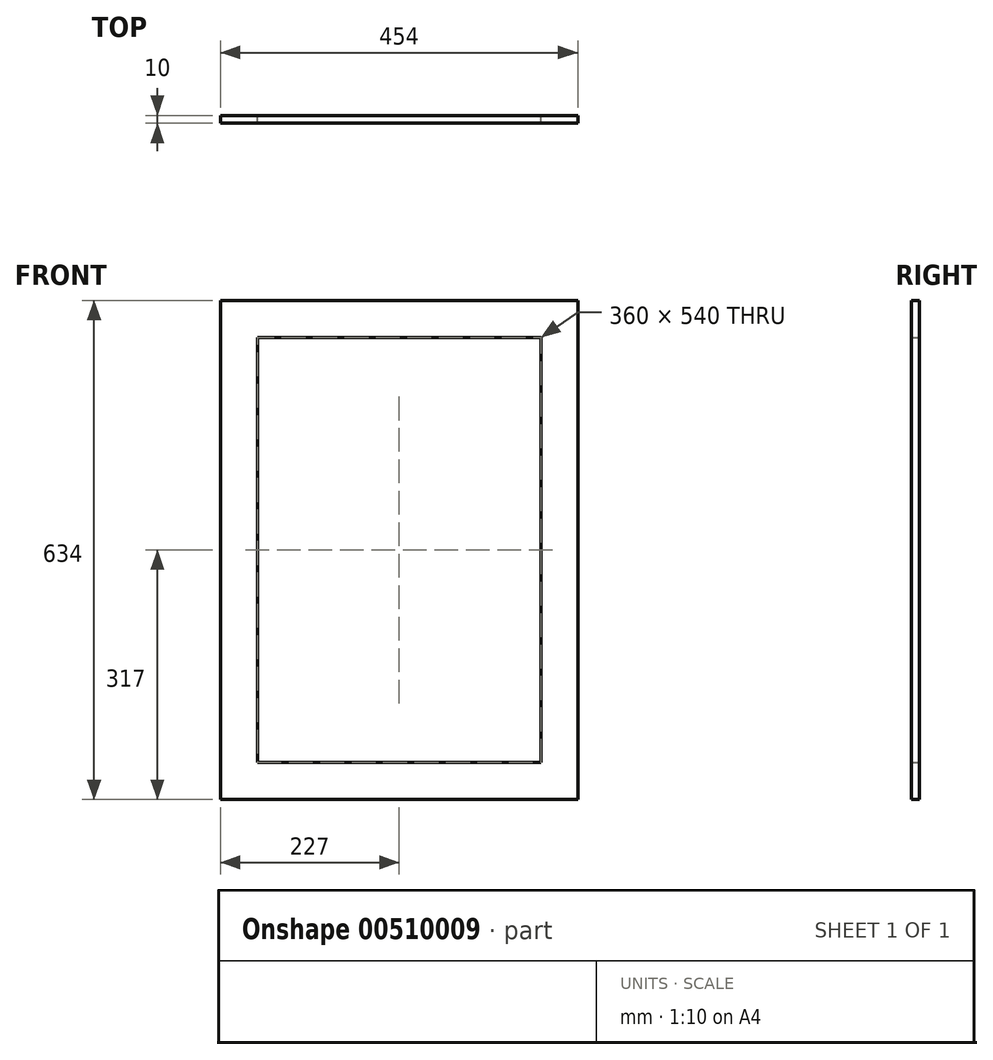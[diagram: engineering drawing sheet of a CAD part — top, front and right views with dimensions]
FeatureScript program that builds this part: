
annotation { "Feature Type Name" : "Feature", "Feature Type Description" : "" }
export const myFeature = defineFeature(function(context is Context, id is Id, definition is map)
    precondition{}
    {
        {
            var Q0;
            Q0=qCreatedBy(makeId("Front.planeOp"),FACE);
            var sketch = newSketch(context, id + "F0", { "sketchPlane" : qUnion([Q0])});
            skLineSegment(sketch, "E0.bottom", {"start": v(-180, 270) * mm, "end": v(180, 270) * mm});
            skLineSegment(sketch, "E0.top", {"start": v(-180, -270) * mm, "end": v(180, -270) * mm});
            skLineSegment(sketch, "E0.left", {"start": v(-180, 270) * mm, "end": v(-180, -270) * mm});
            skLineSegment(sketch, "E0.right", {"start": v(180, 270) * mm, "end": v(180, -270) * mm});
            skLineSegment(sketch, "E1", {"start": v(-180, 270) * mm, "end": v(180, -270) * mm, "construction": true});
            skLineSegment(sketch, "E2.0", {"start": v(-227, 317) * mm, "end": v(227, 317) * mm});
            skLineSegment(sketch, "E2.1", {"start": v(-227, 317) * mm, "end": v(-227, -317) * mm});
            skLineSegment(sketch, "E2.2", {"start": v(-227, -317) * mm, "end": v(227, -317) * mm});
            skLineSegment(sketch, "E2.3", {"start": v(227, 317) * mm, "end": v(227, -317) * mm});
            skSolve(sketch);
        }
        {
            var Q0;
            Q0=qSketchRegion(id+"F0",true);
            extrude(context, id + "F1", {"entities" : qUnion([Q0]), "depth" : 10 * mm});
        }
    });
